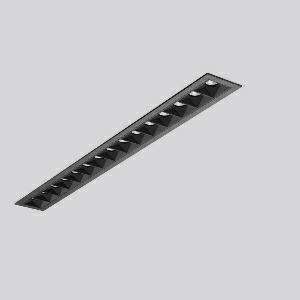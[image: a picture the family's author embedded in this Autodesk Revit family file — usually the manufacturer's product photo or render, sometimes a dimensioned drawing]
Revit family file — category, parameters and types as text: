
# Revit family: beamline_slim_641330_003_2_76_6d76
name_source: partatom
category: Lighting Fixtures
units: mm (PartAtom-declared; Revit-internal decimal feet)

## family parameters
Cut with Voids When Loaded = No
Host = Face
Light Source = No
Part Type = Normal
Room Calculation Point = No
Round Connector Dimension = Use Diameter
Shared = No

## types (1)
- BEAMLINE SLIM (1 x LED Modul 940, 3250 lm, 4000)
    Apparent Load = 36 VA
    CIE Flux Codes = 100 100 100 100 100
    Color Rendering = 92
    Color Temperature = 4000
    Default Elevation = 1800 mm
    Description = Series: BEAMLINE SLIM
Minimalistic recessed ceiling luminaire for aesthetically sophisticated lighting. Housing: metal, powder-coated. Perfect heat management with an aluminium heat sink. LED light unit with MRS technology: Mini-Reflector-System made of metallised thermoplastic with prismatic black glare-suppressing frame for pleasant glare-free light (RUG < 10). Medium beam light distribution. Ceiling installation with spring system. Including separate LED converter with connecting cable 450 mm. 
Colour: deep black, matt (RAL 9005)
Length: 435 mm
Width: 45 mm
Height: 1.5 mm
Cut-out length: 430 mm
Cut-out width: 40 mm
Recess height: 110 mm
Luminaire: recess height: 60 mm
Lamp: LED
Socket: without socket
Colour temperature: 4000K
Colour rendering index (CRI): 90
System power: 36 W
Rated luminous flux: 3250 lm
Luminous efficiency: 90 lm/W
Control gear: Converter, dimmable, DALI
Protection class: II
Type of protection: IP 20
    Height = 0 mm  [stored 0 ft]
    Lamp = 1 x LED Modul 940
    Lamp Light Flux = 3250 lm
    Lamp count = 1
    Length = 435 mm
    Lifetime = 50000 h
    Luminous efficacy = 90 lm/W
    Manufacturer = RZB
    ModVariant = No
    Model = 641330.003.2.76
    Mounting Place = Ceiling
    Mounting Type = Recessed
    Number of Poles = 1
    OnlyDefault = Yes
    Power Factor = 1
    Product Name = BEAMLINE SLIM
    Product group = Recessed LED linear luminaires
    ProductGroupID = 407
    Protection Class = Protection class II
    Protection Degree = IP 20
    RLX_Detail_Level = 1
    RLX_Emergency_Light_Flux = 0 lm
    RLX_Emergency_Type = 0
    RLX_Emergency_Type_DB = No
    RlxData = <blob elided: 19869 chars, md5=288a064f>
    Socket = socket
    Standby Power = 0 W
    System Light Flux = 3250 lm
    System Power = 36 W
    Type Comments = Product without accessories
    Type Image = 641329.003.jpg
    URL = http://relux.com
    VarID = ---
    Voltage = 230 V
    Voltage Range = 220-240 V
    Weight = 0.00 kg
    Width = 45 mm

note: [stored X ft] marks values corroborated as IEEE doubles in the binary element streams (Revit-internal decimal feet)

## geometry (parser evidence)
native form markers: Blend x4, Sweep x11
no freeform markers — native parametric forms only
